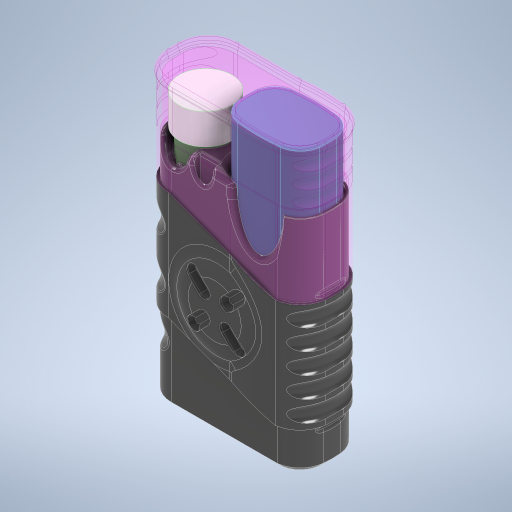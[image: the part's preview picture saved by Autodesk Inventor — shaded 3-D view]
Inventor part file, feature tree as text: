
AUTODESK INVENTOR PART (.ipt)
format: ipt  version: 2024.1 (Build 281209000, 209)  size: 3,728,896 bytes
history: native  units: mm
features: fillet x35, projected_geometry x33, extrude x26, sketch x14, other x6, revolve x6, sweep x2, pattern_circular x2, chamfer x2, plane x1, mirror x1
ambient origin geometry x8: Origin, YZ Plane, XZ Plane, XY Plane, X Axis, Y Axis, Z Axis, Center Point
bodies: Body1 (feature_tree), Body2 (feature_tree), Body3 (feature_tree), Body4 (feature_tree)
feature tree (128):
  other  "vape"
  extrude  "Extrusion1"  Depth=8.35mm
  fillet  "Fillet1"  Radius=80.0mm
  extrude  "Extrusion2"  Depth=11.6mm TaperAngle=0.0deg
  plane  "Work Plane1"
  extrude  "Extrusion3"  Depth=45.8mm TaperAngle=0.0deg
  extrude  "Extrusion4"  Depth=22.1mm
  extrude  "Extrusion5"  Depth=1.5mm
  extrude  "Extrusion6"  Depth=1.5mm
  fillet  "Fillet2"  Radius=1.5mm
  extrude  "Extrusion8"  Depth=15.55mm
  extrude  "Extrusion20"  Depth=3.0mm
  extrude  "Extrusion21"  Depth=3.0mm
  sweep  "Sweep2"
  extrude  "Extrusion22"  Depth=13.0mm
  fillet  "Fillet22"  Radius=2.0mm
  fillet  "Fillet23"  Radius=10.0mm
  fillet  "Fillet24"  Radius=11.0mm
  fillet  "Fillet25"  Radius=6.0mm
  fillet  "Fillet26"  Radius=2.0mm
  fillet  "Fillet4"  Radius=3.0mm
  extrude  "Extrusion10"  Depth=2.4mm
  extrude  "Extrusion11"  Depth=7.3mm
  fillet  "Fillet10"  Radius=7.0mm
  fillet  "Fillet27"  Radius=45.0mm
  extrude  "Extrusion13"  Depth=0.25mm
  fillet  "Fillet28"  Radius=71.0mm
  extrude  "vapeLID"  Depth=71.0mm TaperAngle=0.0deg
  extrude  "Extrusion15"  Depth=3.0mm TaperAngle=30.0deg
  fillet  "Fillet29"  Radius=1.0mm
  extrude  "Extrusion25"  Depth=15.0mm TaperAngle=0.0deg
  fillet  "Fillet30"  Radius=15.0mm
  other  "Work Axis1"
  sketch  "Sketch29"  dims[d28=17.0mm d29=45.8mm d30=0.0mm]
  revolve  "Revolution1"  [1 undecoded]
  sketch  "Sketch30"  dims[d31=17.0mm d38=22.1mm]
  revolve  "Revolution2"  [1 undecoded]
  fillet  "Fillet32"  Radius=15.0mm
  extrude  "Extrusion26"  Depth=15.780931mm
  revolve  "Revolution3"  [1 undecoded]
  revolve  "Revolution5"  [1 undecoded]
  extrude  "Extrusion27"  Depth=7.5mm
  extrude  "Extrusion28"  Depth=6.0mm
  fillet  "Fillet34"  Radius=3.0mm
  other  "Work Axis2"
  revolve  "Revolution6"  [1 undecoded]
  pattern_circular  "Circular Pattern1"  [2 undecoded]
  extrude  "Extrusion29"  Depth=1.0mm
  fillet  "Fillet35"  Radius=0.5mm
  fillet  "Fillet36"  Radius=1.0mm
  fillet  "Fillet37"  Radius=24.0mm
  fillet  "Fillet38"  Radius=2.5mm
  fillet  "Fillet39"  Radius=0.7mm
  fillet  "Fillet40"  Radius=3.0mm
  fillet  "Fillet41"  Radius=5.0mm
  pattern_circular  "Circular Pattern2"  [2 undecoded]
  fillet  "Fillet42"  Radius=1.5mm
  fillet  "Fillet43"  Radius=6.0mm
  fillet  "Fillet45"  Radius=3.65mm
  fillet  "Fillet46"  Radius=10.0mm
  extrude  "Extrusion30"  Depth=1.5mm
  extrude  "Extrusion35"  Depth=14.0mm
  fillet  "Fillet53"  Radius=19.0mm
  fillet  "Fillet54"  [1 undecoded]
  fillet  "Fillet55"  Radius=7.8mm
  chamfer  "Chamfer2"  Distance=8.0mm
  mirror  "Mirror1"
  fillet  "Fillet56"  Radius=7.8mm
  fillet  "Fillet57"  Radius=7.8mm
  extrude  "Extrusion31"  Depth=7.8mm
  extrude  "Extrusion32"  TaperAngle=0.0deg  [1 undecoded]
  sketch  "Sketch48"  dims[d48=3.0mm d49=3.0mm]
  sweep  "Sweep3"
  revolve  "Revolution8"  [1 undecoded]
  fillet  "Fillet48"  Radius=18.25mm
  chamfer  "Chamfer3"  Distance=6.0mm
  extrude  "Extrusion33"  Depth=6.0mm
  extrude  "Extrusion34"  Depth=6.0mm
  fillet  "Fillet49"  [1 undecoded]
  fillet  "Fillet50"  Radius=3.0mm
  fillet  "Fillet51"  Radius=6.0mm
  other  "vape-tube"
  other  "storage"
  projected_geometry  "Projected Loop2"
  projected_geometry  "Projected Loop3"
  projected_geometry  "Projected Loop4"
  projected_geometry  "Projected Loop6"
  other  "vape-lid"
  projected_geometry  "Projected Loop13"
  sketch  "Sketch23"  dims[d4=98.5mm d5=0.0mm d9=8.35mm d22=80.0mm d23=0.0mm]
  projected_geometry  "Projected Loop14"
  sketch  "Sketch25"  dims[d24=20.0mm d26=11.6mm d27=0.0mm]
  projected_geometry  "Projected Loop15"
  sketch  "Sketch37"  dims[d39=31.1mm d41=1.5mm]
  projected_geometry  "Projected Loop32"
  projected_geometry  "Projected Loop33"
  projected_geometry  "Projected Loop34"
  projected_geometry  "Projected Loop35"
  sketch  "Sketch45"  dims[d42=1.5mm d44=1.5mm d45=1.5mm]
  projected_geometry  "Projected Loop36"
  projected_geometry  "Projected Loop37"
  projected_geometry  "Projected Loop38"
  projected_geometry  "Projected Loop39"
  sketch  "Sketch47"  dims[d46=11.05mm d47=15.55mm]
  sketch  "Sketch49"  dims[d50=3.0mm d51=3.0mm]
  sketch  "3D Sketch1"
  sketch  "Sketch51"  dims[d52=11.05mm d53=15.55mm]
  sketch  "Sketch52"  dims[d54=2.5mm d55=13.0mm]
  projected_geometry  "Projected Loop53"
  sketch  "Sketch53"  dims[d56=12.5mm d57=60.0mm d58=0.0mm d59=2.0mm d60=10.0mm d61=0.0mm d62=11.0mm d66=6.0mm d67=0.0mm d69=2.0mm d83=3.0mm]
  projected_geometry  "Projected Loop60"
  projected_geometry  "Projected Loop61"
  projected_geometry  "Projected Loop62"
  projected_geometry  "Projected Loop63"
  projected_geometry  "Projected Loop64"
  projected_geometry  "Projected Loop65"
  projected_geometry  "Projected Loop66"
  projected_geometry  "Projected Loop67"
  projected_geometry  "Projected Loop68"
  projected_geometry  "Projected Loop69"
  projected_geometry  "Projected Loop70"
  projected_geometry  "Projected Loop71"
  projected_geometry  "Projected Loop72"
  sketch  "Sketch54"  dims[d86=72.0mm d87=0.0mm d88=2.4mm d89=7.3mm d91=7.0mm d92=45.0mm d93=0.0mm d94=0.25mm d105=71.0mm d106=0.0mm d108=71.0mm d109=0.0mm d110=3.0mm d111=30.0deg d158=1.0mm d159=15.0mm d160=0.0mm d161=15.0mm d162=0.0mm d163=0.0mm d164=0.0mm d169=0.0mm d170=0.0mm d171=15.0mm d172=15.780931mm d173=20.0mm d174=9.0mm d175=7.5mm d176=6.0mm d177=3.0mm d178=1.0mm d179=2.0mm d180=1.0mm d181=0.5mm d182=1.0mm d183=24.0mm d184=2.5mm d185=0.7mm d186=3.0mm d187=5.0mm d188=0.5mm d193=1.5mm d194=6.0mm d195=3.65mm d196=10.0mm d197=0.0mm d198=1.5mm d199=14.0mm d200=19.0mm d201=19.0mm d207=180.0deg d208=7.8mm d209=8.0mm d210=7.8mm d211=7.8mm d212=7.8mm d215=0.0mm d216=180.0deg d218=1.5mm d221=18.25mm d222=0.0mm d225=6.0mm d226=6.0mm d229=6.0mm d230=180.0deg d240=3.0mm d241=6.0mm d242=6.0mm d243=6.0mm d245=12.0mm d247=180.0deg d249=20.0mm d253=22.0mm d254=22.0mm d255=25.0mm d256=1.0mm d257=1.0mm d258=0.0mm d259=1.0mm d260=0.0mm d261=0.2mm d263=5.0mm d264=10.0mm d266=10.0mm d267=30.0mm d268=4.0mm d269=45.0deg d270=40.0mm d271=360.0deg d275=0.4mm d276=1.1mm d277=2.4mm d278=3.0mm d279=1.5mm d280=3.0mm d281=0.810487mm d282=2.943591mm d283=4.5mm d284=0.0mm d285=2.0mm d286=0.7mm d287=3.0mm d288=0.5mm d289=1.0mm d290=1.0mm d291=1.0mm d292=40.0mm d293=360.0deg d295=1.0mm d296=0.4mm d298=1.0mm d299=0.4mm d312=12.0mm d315=8.5mm d316=8.5mm d317=5.0mm d318=40.0mm d320=360.0deg d322=10.0mm d323=0.8mm d324=0.0mm d325=0.0mm d329=1.5mm d330=2.0mm d331=45.0deg d332=21.0mm d334=5.458726mm d335=20.0mm d336=30.0mm d337=42.5mm d338=30.0mm d339=0.0mm d340=15.0mm d341=0.0mm d342=0.0mm d343=0.0mm d344=30.754897mm d349=22.0mm d350=24.0mm d351=180.0deg d352=2.0mm d353=2.0mm d354=15.0mm d355=45.0deg d365=1.5mm d366=1.5mm d367=15.0mm d368=0.0mm d369=1.5mm d370=0.25mm d371=0.25mm d372=1.4mm d375=7.5mm d376=0.0mm d377=0.4mm d378=0.4mm d385=25.089685mm d387=0.5mm d388=12.0mm d389=6.0mm d390=6.0mm d391=1.5mm d392=1.5mm d396=0.25mm d397=1.5mm d398=0.25mm d399=1.5mm d400=1.6mm d402=33.5mm d403=1.5mm d404=0.0mm d405=16.0mm d406=11.0mm d407=8.0mm d408=11.5mm d409=8.0mm]
  projected_geometry  "Projected Loop73"
  projected_geometry  "Projected Loop74"
  projected_geometry  "Projected Loop75"
  projected_geometry  "Projected Loop76"
note: 13 required parameter values undecoded (feature->parameter linkage not recoverable at this tier; creation-order binding heuristic only, values carry confidence <= 0.55)